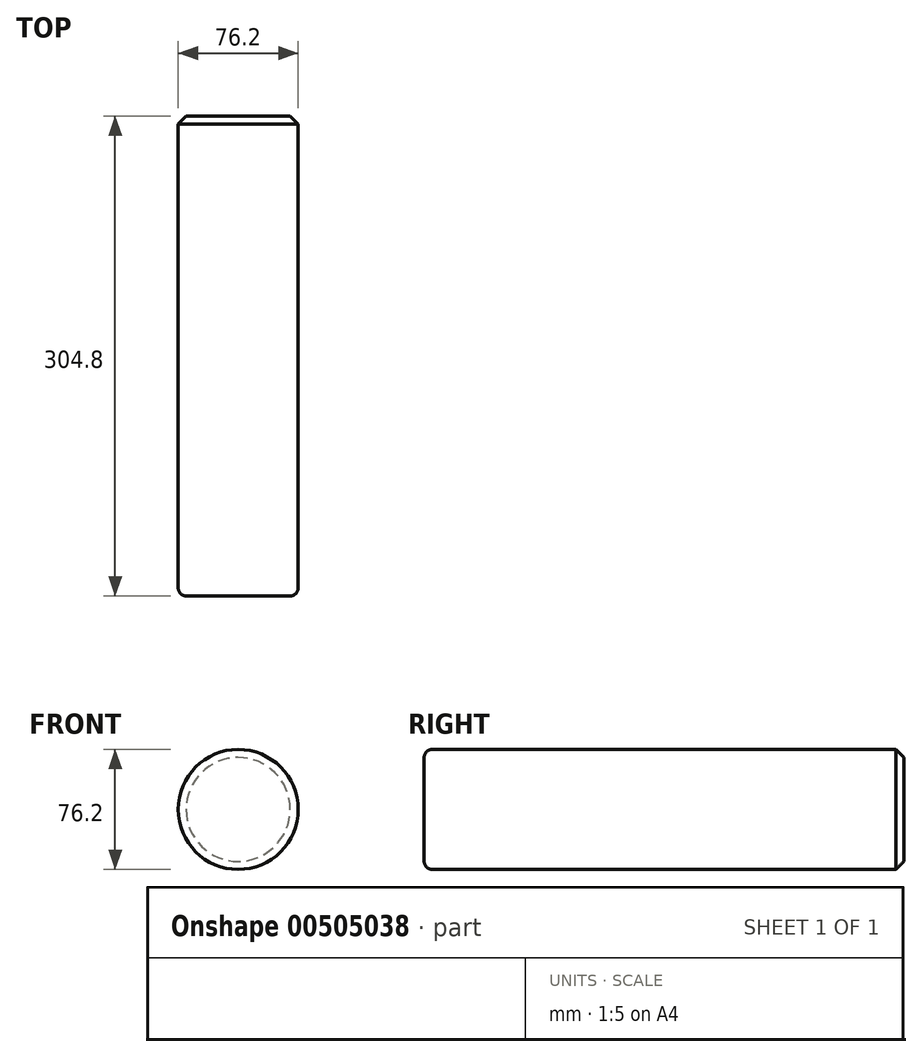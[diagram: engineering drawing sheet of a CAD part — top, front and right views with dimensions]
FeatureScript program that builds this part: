
annotation { "Feature Type Name" : "Feature", "Feature Type Description" : "" }
export const myFeature = defineFeature(function(context is Context, id is Id, definition is map)
    precondition{}
    {
        {
            var Q0;
            Q0=qCreatedBy(makeId("Front.planeOp"),FACE);
            var sketch = newSketch(context, id + "F0", { "sketchPlane" : qUnion([Q0])});
            skCircle(sketch, "E0", {"center": v(0, 0) * mm, "radius": 38.1 * mm});
            skSolve(sketch);
        }
        {
            var Q0;
            Q0=makeQuery(id+"F0.imprint","IMPRINT",FACE,{"disambiguationData":[TD([[makeQuery(id+"F0.imprint","IMPRINT",EDGE,{"derivedFrom":sQuery(id+"F0.wireOp",EDGE,"E0")}),1.0]])]});
            extrude(context, id + "F1", {"entities" : qUnion([Q0]), "endBound" : BoundingType.SYMMETRIC, "offsetDistance" : 25.4 * mm, "depth" : 304.8 * mm});
        }
        {
            var Q0;
            Q0=makeQuery(id+"F1.opExtrude","CAP_EDGE",EDGE,{"disambiguationData":[OSD([sQuery(id+"F0.wireOp",EDGE,"E0")])],"isStart":false});
            fillet(context, id + "F2", {"entities" : qUnion([Q0]), "radius" : 5.08 * mm, "tangentPropagation" : true, "allowEdgeOverflow" : false});
        }
        {
            var Q0;
            Q0=makeQuery(id+"F1.opExtrude","SWEPT_FACE",FACE,{"disambiguationData":[OSD([sQuery(id+"F0.wireOp",EDGE,"E0")])]});
            chamfer(context, id + "F3", {"entities" : qUnion([Q0]), "width" : 5.08 * mm, "tangentPropagation" : true});
        }
    });
